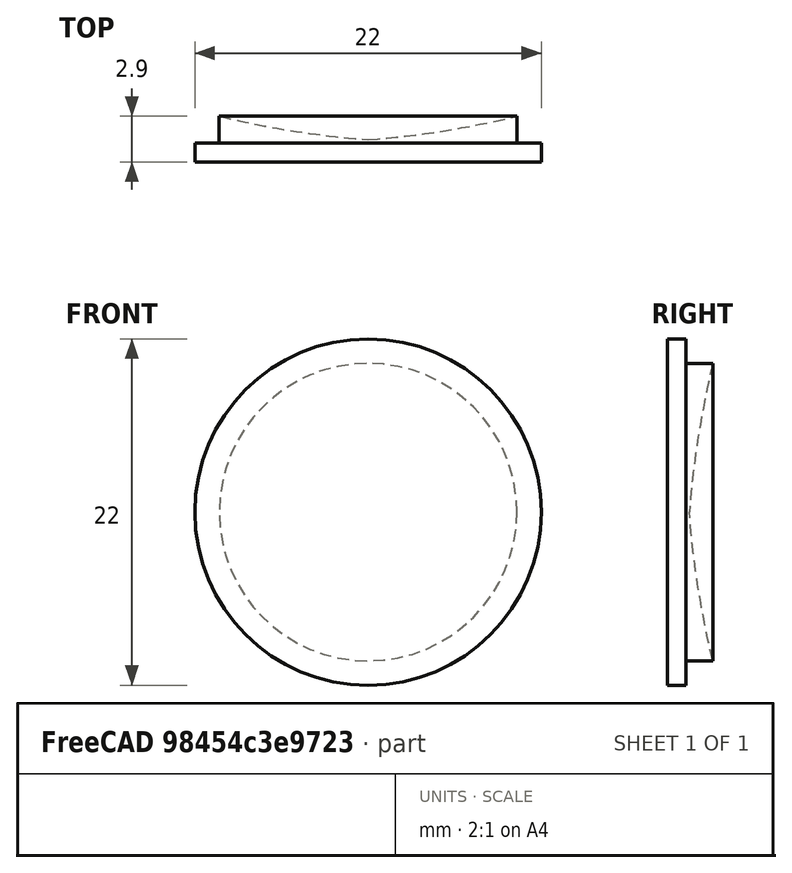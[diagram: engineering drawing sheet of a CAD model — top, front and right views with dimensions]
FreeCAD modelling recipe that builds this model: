
FCSTD DOCUMENT  (FreeCAD 0.20R29603 (Git))
Label: tipka_2x
License: All rights reserved
LicenseURL: http://en.wikipedia.org/wiki/All_rights_reserved
objects: Sketcher::SketchObject×1, PartDesign::Revolution×1, PartDesign::Body×1
note: 4 computed .brp shape members not serialized (recipe doc carries the construction recipe); baked Part::Feature solids carry a one-line shape summary decoded from their .brp

FEATURE [Sketcher::SketchObject] Sketch
  FullyConstrained = true
  MapMode = 5
  Support = -> [XY_Plane]
  sketch-geometry (6):
    g0: LineSegment StartX=0 StartY=0 StartZ=0 EndX=11 EndY=0 EndZ=0
    g1: LineSegment StartX=11 StartY=0 StartZ=0 EndX=11 EndY=1.2 EndZ=0
    g2: LineSegment StartX=11 StartY=1.2 StartZ=0 EndX=9.45 EndY=1.2 EndZ=0
    g3: LineSegment StartX=9.45 StartY=1.2 StartZ=0 EndX=9.45 EndY=2.9 EndZ=0
    g4: ArcOfCircle CenterX=-4.6511 CenterY=61.2195 CenterZ=0 NormalX=0 NormalY=0 NormalZ=1 AngleXU=0 Radius=60 StartAngle=4.78999 EndAngle=4.94963
    g5: LineSegment StartX=0 StartY=0 StartZ=0 EndX=-1.24e-14 EndY=1.4 EndZ=0
  constraints (18):
    c: Coincident(g-1,g0)
    c: PointOnObject(g0,g-1)
    c: Coincident(g0,g1)
    c: Vertical(g1)
    c: Coincident(g1,g2)
    c: Horizontal(g2)
    c: Coincident(g2,g3)
    c: Vertical(g3)
    c: Coincident(g4,g3)
    c: PointOnObject(g4,g-2)
    c: DistanceX(g0,g0) = 11
    c: DistanceY(g1,g1) = 1.2
    c: DistanceY(g3,g3) = 1.7
    c: Coincident(g5,g0)
    c: Coincident(g5,g4)
    c: DistanceY(g5,g5) = 1.4
    c: Radius(g4) = 60
    c: DistanceX(g0,g3) = 9.45
FEATURE [PartDesign::Revolution] Revolution
  Angle = 360
  Axis = (0,1,0)
  Base = (0,0,0)
  Profile = -> Sketch
  ReferenceAxis = -> Sketch [V_Axis]
  Reversed = true
FEATURE [PartDesign::Body] Body
  Group = -> [Sketch,Revolution]
  Origin = -> Origin
  Tip = -> Revolution
